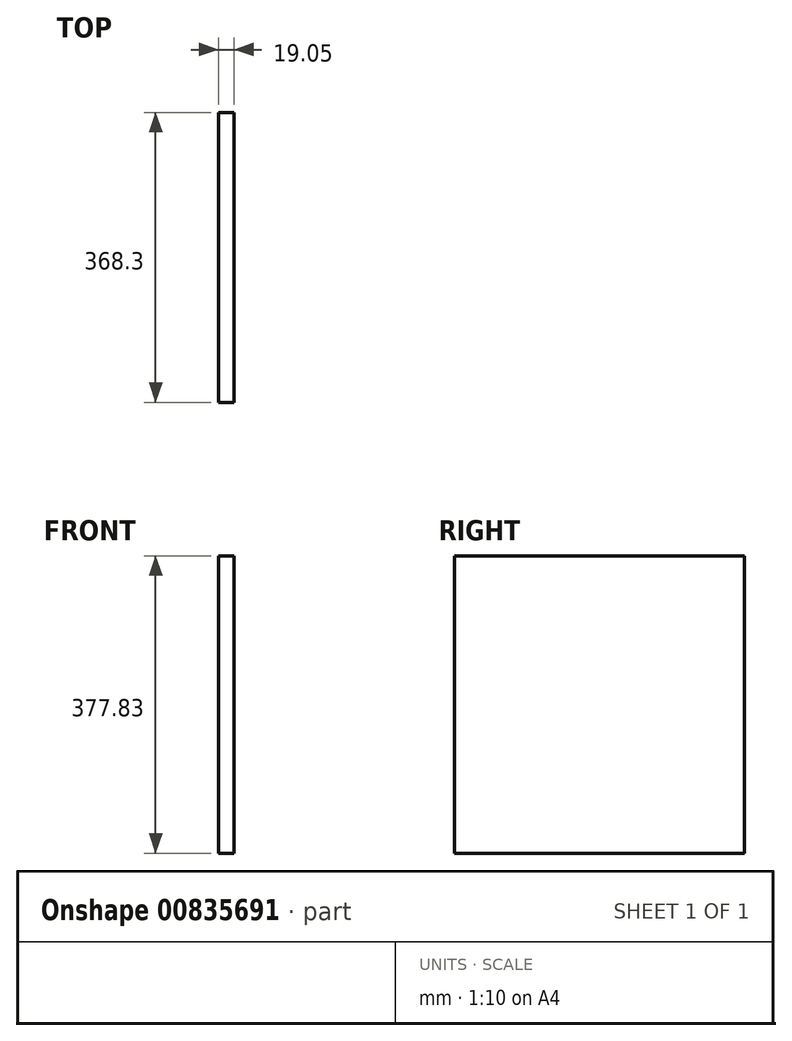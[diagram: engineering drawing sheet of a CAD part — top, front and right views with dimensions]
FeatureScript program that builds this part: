
annotation { "Feature Type Name" : "Feature", "Feature Type Description" : "" }
export const myFeature = defineFeature(function(context is Context, id is Id, definition is map)
    precondition{}
    {
        {
            var Q0;
            Q0=qCreatedBy(makeId("Right.planeOp"),FACE);
            var sketch = newSketch(context, id + "F0", { "sketchPlane" : qUnion([Q0])});
            skLineSegment(sketch, "E0.bottom", {"start": v(0, 0) * mm, "end": v(368.3, 0) * mm});
            skLineSegment(sketch, "E0.top", {"start": v(0, 377.83) * mm, "end": v(368.3, 377.83) * mm});
            skLineSegment(sketch, "E0.left", {"start": v(0, 0) * mm, "end": v(0, 377.83) * mm});
            skLineSegment(sketch, "E0.right", {"start": v(368.3, 0) * mm, "end": v(368.3, 377.83) * mm});
            skSolve(sketch);
        }
        {
            var Q0;
            Q0=qSketchRegion(id+"F0",true);
            extrude(context, id + "F1", {"entities" : qUnion([Q0]), "depth" : 19.05 * mm, "offsetDistance" : 25.4 * mm});
        }
    });
